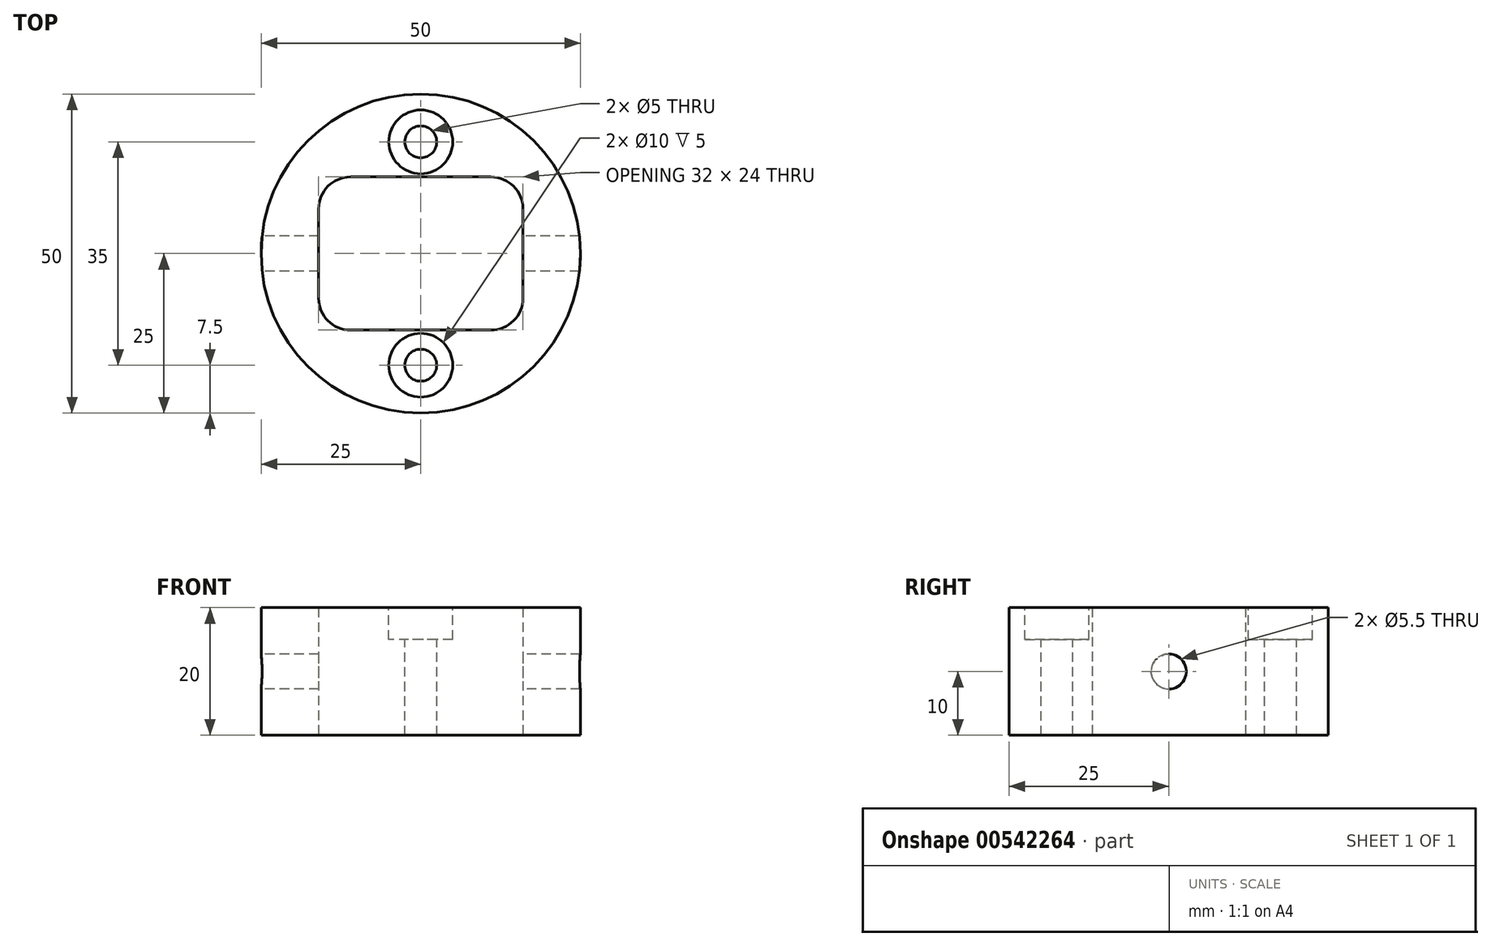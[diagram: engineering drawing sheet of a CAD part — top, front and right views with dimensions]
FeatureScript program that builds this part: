
annotation { "Feature Type Name" : "Feature", "Feature Type Description" : "" }
export const myFeature = defineFeature(function(context is Context, id is Id, definition is map)
    precondition{}
    {
        {
            var Q0;
            Q0=qCreatedBy(makeId("Top.planeOp"),FACE);
            var sketch = newSketch(context, id + "F0", { "sketchPlane" : qUnion([Q0])});
            skCircle(sketch, "E0", {"center": v(0, 0) * mm, "radius": 25 * mm});
            skCircle(sketch, "E1", {"center": v(0, 0) * mm, "radius": 20 * mm, "construction": true});
            skLineSegment(sketch, "E2.bottom", {"start": v(-16, -12) * mm, "end": v(16, -12) * mm});
            skLineSegment(sketch, "E2.top", {"start": v(-16, 12) * mm, "end": v(16, 12) * mm});
            skLineSegment(sketch, "E2.left", {"start": v(-16, -12) * mm, "end": v(-16, 12) * mm});
            skLineSegment(sketch, "E2.right", {"start": v(16, -12) * mm, "end": v(16, 12) * mm});
            skSolve(sketch);
        }
        {
            var Q0;
            Q0=makeQuery(id+"F0.imprint","IMPRINT",FACE,{"disambiguationData":[TD([[makeQuery(id+"F0.imprint","IMPRINT",EDGE,{"derivedFrom":sQuery(id+"F0.wireOp",EDGE,"E0")}),1.0]])]});
            extrude(context, id + "F1", {"entities" : qUnion([Q0]), "depth" : 20 * mm, "offsetDistance" : 25 * mm});
        }
        {
            var Q0;
            Q0=makeQuery(id+"F1.opExtrude","CAP_FACE",FACE,{"disambiguationData":[OSD([sQuery(id+"F0.wireOp",EDGE,"E0"),sQuery(id+"F0.wireOp",EDGE,"E2.bottom"),sQuery(id+"F0.wireOp",EDGE,"E2.top"),sQuery(id+"F0.wireOp",EDGE,"E2.left"),sQuery(id+"F0.wireOp",EDGE,"E2.right")])],"isStart":false});
            var sketch = newSketch(context, id + "F2", { "sketchPlane" : qUnion([Q0])});
            skLineSegment(sketch, "E3", {"start": v(0, 17.5) * mm, "end": v(0, -17.5) * mm, "construction": true});
            skSolve(sketch);
        }
        {
            var Q0;
            Q0=sQuery(id+"F2.wireOp",VERTEX,"E3.start");
            var Q1;
            Q1=sQuery(id+"F2.wireOp",VERTEX,"E3.end");
            var Q2;
            Q2=makeQuery(id+"F1.opExtrude","SWEPT_BODY",BODY,{"disambiguationData":[OSD([sQuery(id+"F0.wireOp",EDGE,"E0"),sQuery(id+"F0.wireOp",EDGE,"E2.bottom"),sQuery(id+"F0.wireOp",EDGE,"E2.top"),sQuery(id+"F0.wireOp",EDGE,"E2.left"),sQuery(id+"F0.wireOp",EDGE,"E2.right")])]});
            hole(context, id + "F3", {"style" : HoleStyle.C_BORE, "endStyle" : HoleEndStyle.THROUGH, "holeDiameter" : 5 * mm, "cBoreDiameter" : 10 * mm, "cBoreDepth" : 5 * mm, "isTappedThrough" : true, "tappedDepth" : 12 * mm, "tapClearance" : 3, "startFromSketch" : true, "locations" : qUnion([Q0, Q1]), "scope" : qUnion([Q2])});
        }
        {
            var Q0;
            Q0=makeQuery(id+"F1.opExtrude","SWEPT_FACE",FACE,{"disambiguationData":[OSD([sQuery(id+"F0.wireOp",EDGE,"E2.right")])]});
            cPlane(context, id + "F4", {"entities" : qUnion([Q0]), "cplaneType" : CPlaneType.OFFSET, "offset" : 50 * mm, "width" : 150 * mm, "height" : 150 * mm});
        }
        {
            var Q0;
            Q0=qCreatedBy(id+"F4.planeOp",FACE);
            var sketch = newSketch(context, id + "F5", { "sketchPlane" : qUnion([Q0])});
            skLineSegment(sketch, "E4", {"start": v(0, 0) * mm, "end": v(0, 20) * mm, "construction": true});
            skPoint(sketch, "E5", {"position": v(0, 10) * mm});
            skSolve(sketch);
        }
        {
            var Q0;
            Q0=sQuery(id+"F5.wireOp",VERTEX,"E5");
            var Q1;
            Q1=makeQuery(id+"F1.opExtrude","SWEPT_BODY",BODY,{"disambiguationData":[OSD([sQuery(id+"F0.wireOp",EDGE,"E0"),sQuery(id+"F0.wireOp",EDGE,"E2.bottom"),sQuery(id+"F0.wireOp",EDGE,"E2.top"),sQuery(id+"F0.wireOp",EDGE,"E2.left"),sQuery(id+"F0.wireOp",EDGE,"E2.right")])]});
            hole(context, id + "F6", {"style" : HoleStyle.SIMPLE, "endStyle" : HoleEndStyle.THROUGH, "standardTappedOrClearance" : lookupTablePath({ "standard" : "ISO", "fit" : "Normal", "size" : "M5", "type" : "Clearance" }), "standardBlindInLast" : lookupTablePath({ "fit" : "Standard", "standard" : "ISO", "size" : "M5", "type" : "Clearance" }), "holeDiameter" : 5.5 * mm, "isTappedThrough" : true, "tappedDepth" : 12 * mm, "tapClearance" : 3, "startFromSketch" : true, "locations" : qUnion([Q0]), "scope" : qUnion([Q1])});
        }
        {
            var Q0;
            Q0=makeQuery(id+"F1.opExtrude","SWEPT_EDGE",EDGE,{"disambiguationData":[OSD([sQuery(id+"F0.wireOp",EDGE,"E2.top"),sQuery(id+"F0.wireOp",EDGE,"E2.right")])]});
            var Q1;
            Q1=makeQuery(id+"F1.opExtrude","SWEPT_EDGE",EDGE,{"disambiguationData":[OSD([sQuery(id+"F0.wireOp",EDGE,"E2.top"),sQuery(id+"F0.wireOp",EDGE,"E2.left")])]});
            var Q2;
            Q2=makeQuery(id+"F1.opExtrude","SWEPT_EDGE",EDGE,{"disambiguationData":[OSD([sQuery(id+"F0.wireOp",EDGE,"E2.bottom"),sQuery(id+"F0.wireOp",EDGE,"E2.left")])]});
            var Q3;
            Q3=makeQuery(id+"F1.opExtrude","SWEPT_EDGE",EDGE,{"disambiguationData":[OSD([sQuery(id+"F0.wireOp",EDGE,"E2.bottom"),sQuery(id+"F0.wireOp",EDGE,"E2.right")])]});
            fillet(context, id + "F7", {"entities" : qUnion([Q0, Q1, Q2, Q3]), "radius" : 5 * mm, "tangentPropagation" : true, "allowEdgeOverflow" : false});
        }
    });
